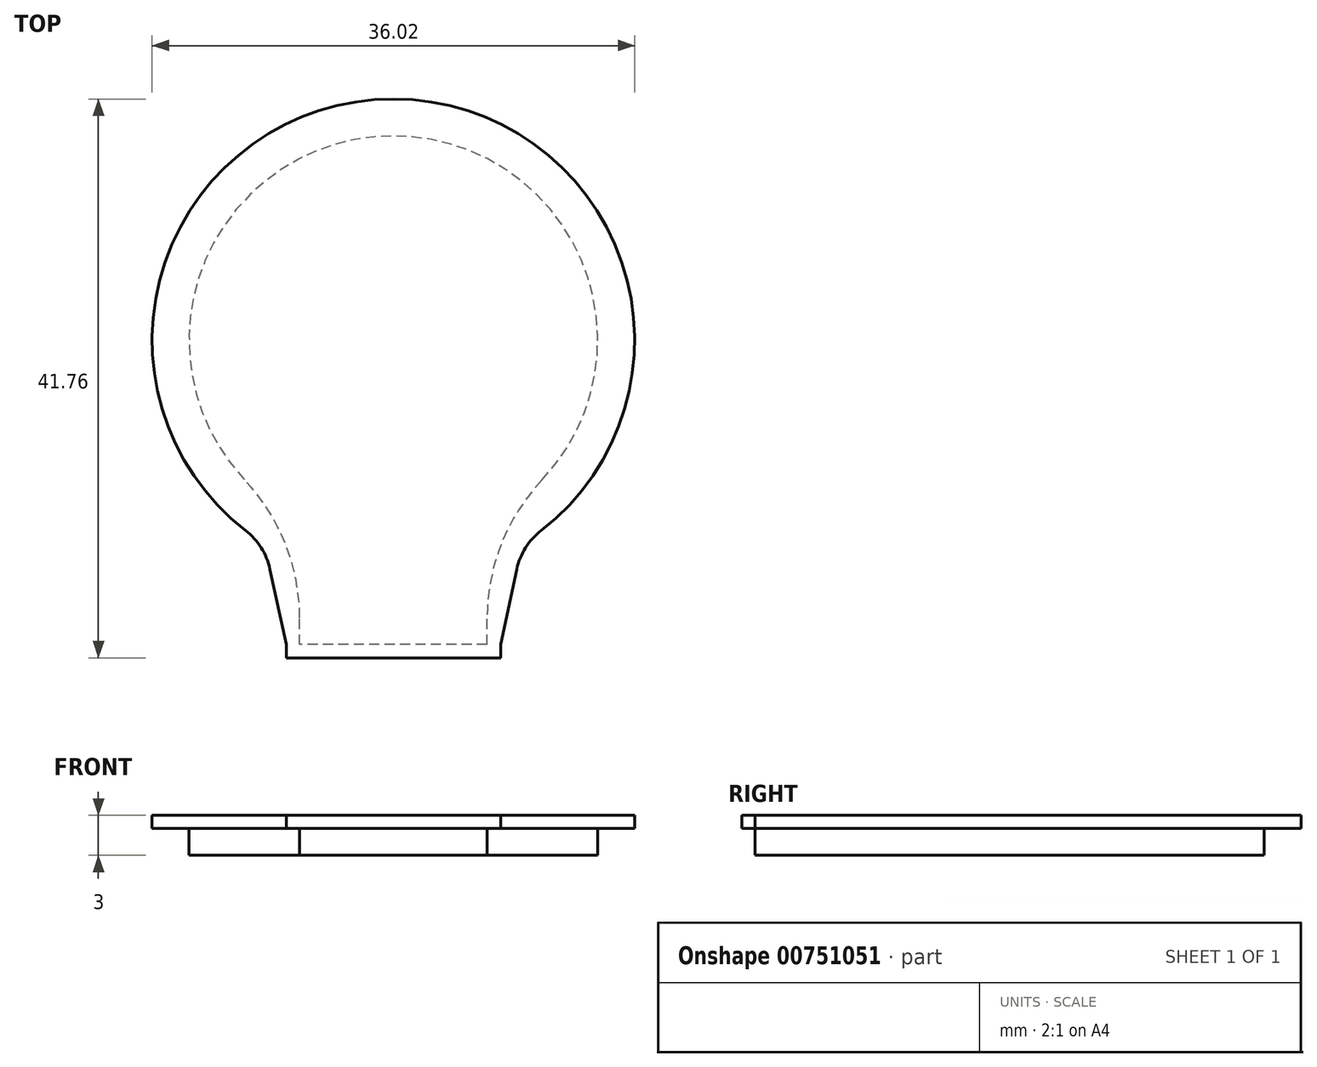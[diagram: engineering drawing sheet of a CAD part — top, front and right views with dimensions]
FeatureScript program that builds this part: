
annotation { "Feature Type Name" : "Feature", "Feature Type Description" : "" }
export const myFeature = defineFeature(function(context is Context, id is Id, definition is map)
    precondition{}
    {
        {
            var Q0;
            Q0=qCreatedBy(makeId("Top.planeOp"),FACE);
            var sketch = newSketch(context, id + "F0", { "sketchPlane" : qUnion([Q0])});
            skArc(sketch, "E0", {"start": v(7, -13.55) * mm, "mid": v(0, 15.25) * mm, "end": v(-7, -13.55) * mm});
            skLineSegment(sketch, "E1", {"start": v(0, 15.25) * mm, "end": v(0, -22.75) * mm});
            skLineSegment(sketch, "E2", {"start": v(0, -22.75) * mm, "end": v(7, -22.75) * mm});
            skLineSegment(sketch, "E3.MirrorCS", {"start": v(0, -22.75) * mm, "end": v(-7, -22.75) * mm});
            skLineSegment(sketch, "E4", {"start": v(7, -22.75) * mm, "end": v(7, -16.75) * mm});
            skLineSegment(sketch, "E5.MirrorCS", {"start": v(-7, -22.75) * mm, "end": v(-7, -16.75) * mm});
            skLineSegment(sketch, "E6", {"start": v(-7, -16.75) * mm, "end": v(-7, -13.55) * mm});
            skLineSegment(sketch, "E7", {"start": v(7, -16.75) * mm, "end": v(7, -13.55) * mm});
            skSolve(sketch);
        }
        {
            var Q0;
            Q0=qSketchRegion(id+"F0",true);
            extrude(context, id + "F1", {"entities" : qUnion([Q0]), "depth" : 2 * mm, "offsetDistance" : 25 * mm});
        }
        {
            var Q0;
            Q0=makeQuery(id+"F1.opExtrude","SWEPT_EDGE",EDGE,{"disambiguationData":[OSD([sQuery(id+"F0.wireOp",EDGE,"E0"),sQuery(id+"F0.wireOp",EDGE,"E6")])]});
            fillet(context, id + "F2", {"entities" : qUnion([Q0]), "radius" : 15 * mm, "tangentPropagation" : true, "allowEdgeOverflow" : false});
        }
        {
            var Q0;
            Q0=makeQuery(id+"F1.opExtrude","SWEPT_EDGE",EDGE,{"disambiguationData":[OSD([sQuery(id+"F0.wireOp",EDGE,"E0"),sQuery(id+"F0.wireOp",EDGE,"E7")])]});
            fillet(context, id + "F3", {"entities" : qUnion([Q0]), "radius" : 15 * mm, "tangentPropagation" : true, "allowEdgeOverflow" : false});
        }
        {
            var Q0;
            Q0=makeQuery(id+"F1.opExtrude","CAP_FACE",FACE,{"disambiguationData":[OSD([sQuery(id+"F0.wireOp",EDGE,"E0"),sQuery(id+"F0.wireOp",EDGE,"E2"),sQuery(id+"F0.wireOp",EDGE,"E3.MirrorCS"),sQuery(id+"F0.wireOp",EDGE,"E4"),sQuery(id+"F0.wireOp",EDGE,"E5.MirrorCS"),sQuery(id+"F0.wireOp",EDGE,"E6"),sQuery(id+"F0.wireOp",EDGE,"E7")])],"isStart":false});
            var sketch = newSketch(context, id + "F4", { "sketchPlane" : qUnion([Q0])});
            skCircle(sketch, "E8", {"center": v(0, 0) * mm, "radius": 18 * mm});
            skLineSegment(sketch, "E9", {"start": v(9.62, -15.22) * mm, "end": v(7, -22.75) * mm});
            skPoint(sketch, "E9.startSnap0", {"position": v(8.06, -15.22) * mm});
            skLineSegment(sketch, "E10", {"start": v(7, -22.75) * mm, "end": v(-7, -22.75) * mm});
            skLineSegment(sketch, "E11", {"start": v(-7, -22.75) * mm, "end": v(-9.62, -15.22) * mm});
            skPoint(sketch, "E11.endSnap0", {"position": v(-8.06, -15.22) * mm});
            skLineSegment(sketch, "E12", {"start": v(-7, -22.75) * mm, "end": v(-7, -23.75) * mm});
            skLineSegment(sketch, "E13", {"start": v(-7, -23.75) * mm, "end": v(7, -23.75) * mm});
            skLineSegment(sketch, "E14", {"start": v(7, -23.75) * mm, "end": v(7, -22.75) * mm});
            skLineSegment(sketch, "E15", {"start": v(-9.62, -15.22) * mm, "end": v(-7, -23.75) * mm});
            skLineSegment(sketch, "E16", {"start": v(7, -23.75) * mm, "end": v(9.62, -15.22) * mm});
            skLineSegment(sketch, "E17", {"start": v(-7, -23.75) * mm, "end": v(-8, -23.75) * mm});
            skLineSegment(sketch, "E18", {"start": v(-8, -23.75) * mm, "end": v(-8, -22.75) * mm});
            skLineSegment(sketch, "E19", {"start": v(-8, -22.75) * mm, "end": v(-9.62, -15.22) * mm});
            skLineSegment(sketch, "E20.MirrorCS", {"start": v(7, -23.75) * mm, "end": v(8, -23.75) * mm});
            skLineSegment(sketch, "E21.MirrorCS", {"start": v(8, -23.75) * mm, "end": v(8, -22.75) * mm});
            skLineSegment(sketch, "E22.MirrorCS", {"start": v(8, -22.75) * mm, "end": v(9.62, -15.22) * mm});
            skSolve(sketch);
        }
        {
            var Q0;
            Q0 = qSketchRegion(id + "F4", true);
            extrude(context, id + "F5", {"entities" : qUnion([Q0]), "operationType" : NewBodyOperationType.ADD, "depth" : 1 * mm, "offsetDistance" : 25 * mm});
        }
        {
            var Q0;
            Q0=makeQuery(id+"F5.opExtrude","SWEPT_EDGE",EDGE,{"disambiguationData":[OSD([sQuery(id+"F4.wireOp",EDGE,"E8"),sQuery(id+"F4.wireOp",EDGE,"E9"),sQuery(id+"F4.wireOp",EDGE,"E16"),sQuery(id+"F4.wireOp",EDGE,"E22.MirrorCS")])]});
            var Q1;
            Q1=makeQuery(id+"F5.opExtrude","SWEPT_EDGE",EDGE,{"disambiguationData":[OSD([sQuery(id+"F4.wireOp",EDGE,"E8"),sQuery(id+"F4.wireOp",EDGE,"E11"),sQuery(id+"F4.wireOp",EDGE,"E15"),sQuery(id+"F4.wireOp",EDGE,"E19")])]});
            fillet(context, id + "F6", {"entities" : qUnion([Q0, Q1]), "radius" : 5 * mm, "tangentPropagation" : true, "allowEdgeOverflow" : false});
        }
    });
